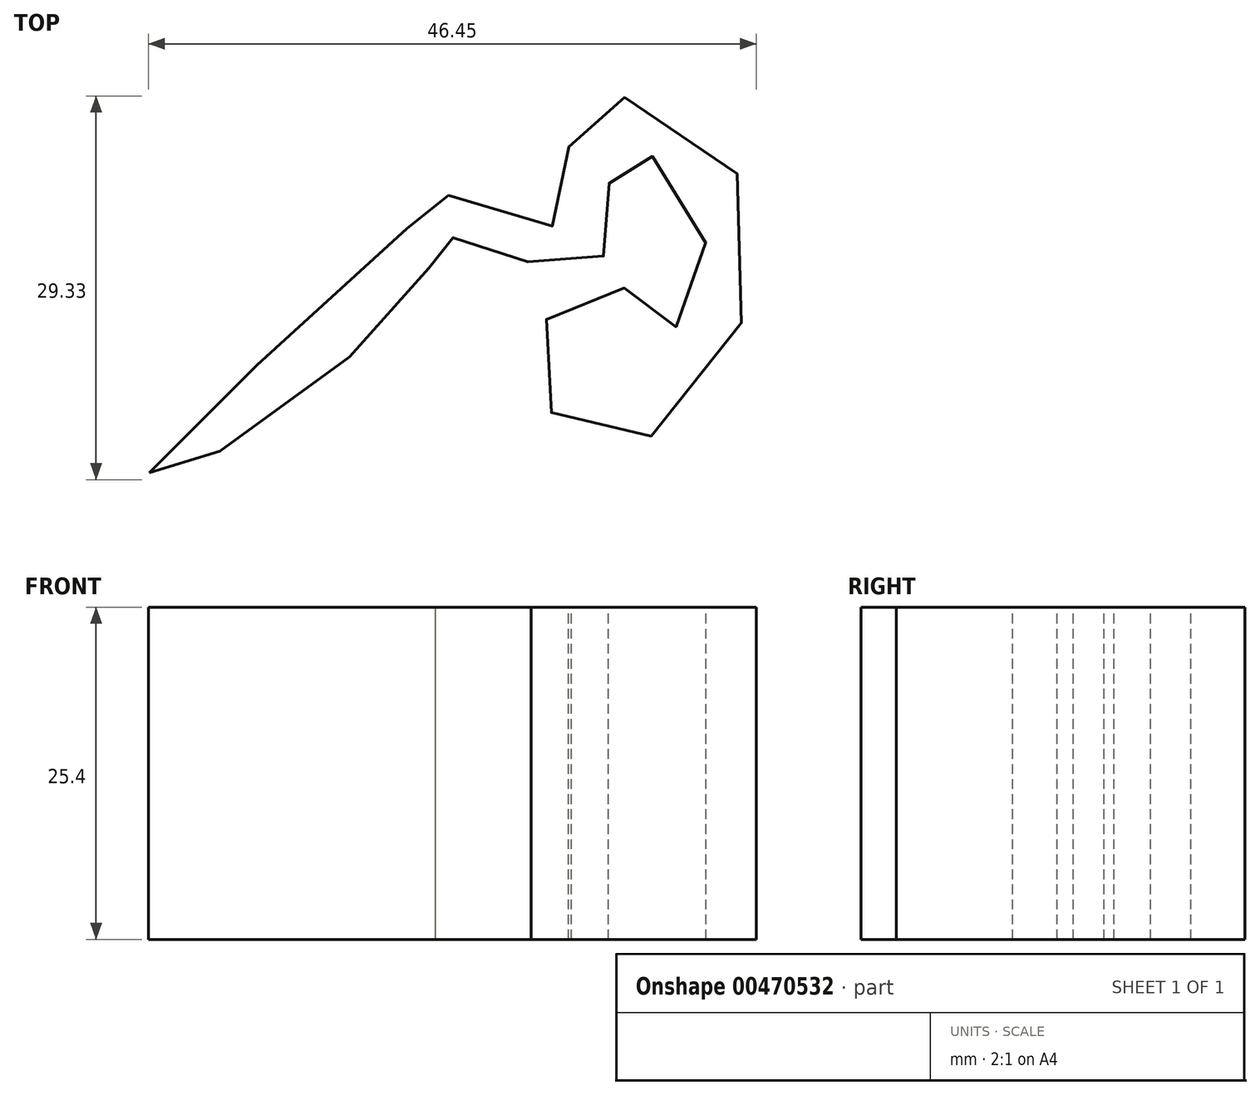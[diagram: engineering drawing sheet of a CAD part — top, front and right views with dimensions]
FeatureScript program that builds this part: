
annotation { "Feature Type Name" : "Feature", "Feature Type Description" : "" }
export const myFeature = defineFeature(function(context is Context, id is Id, definition is map)
    precondition{}
    {
        {
            var Q0;
            Q0=qCreatedBy(makeId("Top.planeOp"),FACE);
            var sketch = newSketch(context, id + "F0", { "sketchPlane" : qUnion([Q0])});
            skLineSegment(sketch, "E0", {"start": v(49.75, 51.2) * mm, "end": v(73.53, 26.54) * mm});
            skLineSegment(sketch, "E1", {"start": v(73.53, 26.54) * mm, "end": v(73.53, 13.22) * mm});
            skLineSegment(sketch, "E2", {"start": v(73.53, 13.22) * mm, "end": v(31.23, 6.67) * mm});
            skLineSegment(sketch, "E3", {"start": v(31.23, 6.67) * mm, "end": v(40.9, 25.8) * mm});
            skLineSegment(sketch, "E4", {"start": v(40.9, 25.8) * mm, "end": v(45.02, 30.55) * mm});
            skLineSegment(sketch, "E5", {"start": v(45.02, 30.55) * mm, "end": v(43.08, 40.77) * mm});
            skLineSegment(sketch, "E6", {"start": v(43.08, 40.77) * mm, "end": v(49.75, 51.2) * mm});
            skFitSpline(sketch, "E7", {"points": [v(18.99, -43.15) * mm, v(40.84, -21.9) * mm, v(40.9, -21.52) * mm, v(50.42, -24.06) * mm, v(51.64, -15.27) * mm, v(64.58, -21.55) * mm, v(55.9, -40.84) * mm, v(48.17, -34.4) * mm, v(54.64, -28.74) * mm, v(58.95, -32.06) * mm, v(61.2, -23.55) * mm, v(55.1, -18.63) * mm, v(54.09, -24.7) * mm, v(52.53, -27.32) * mm, v(42.9, -25.53) * mm, v(41.96, -25.1) * mm, v(41.4, -25.95) * mm, v(30.67, -37.33) * mm, v(18.99, -43.15) * mm]});
            skSolve(sketch);
        }
        {
            var Q0;
            Q0=sQuery(id+"F0.wireOp",EDGE,"E7");
            extrude(context, id + "F1", {"bodyType" : ToolBodyType.SURFACE, "surfaceEntities" : qUnion([Q0]), "depth" : 25.4 * mm});
        }
    });
